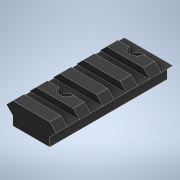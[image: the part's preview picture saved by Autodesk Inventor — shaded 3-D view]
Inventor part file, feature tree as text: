
AUTODESK INVENTOR PART (.ipt)
format: ipt  version: 2021 (Build 250183000, 183)  size: 216,064 bytes
history: native  units: mm
features: extrude x4, sketch x3, pattern_linear x2
ambient origin geometry x8: Origin, YZ Plane, XZ Plane, XY Plane, X Axis, Y Axis, Z Axis, Center Point
bodies: Solid1 (feature_tree)
feature tree (9):
  extrude  "Extrusion1"  Depth=15.67mm
  extrude  "Extrusion3"  Depth=50.0mm TaperAngle=0.0deg
  pattern_linear  "Rectangular Pattern1"  Spacing1=5.25mm  [1 undecoded]
  sketch  "Sketch3"  dims[d9=4.0mm d10=5.25mm d13=10.32mm d14=0.0mm d15=0.0mm d16=200.0mm d18=10.0mm d19=3.2mm d20=6.0mm d21=5.0mm d22=0.0mm d23=0.0mm d24=7.32mm d25=0.0mm d26=70.0mm d28=30.0mm]
  extrude  "Extrusion4"  Depth=30.0mm
  extrude  "Extrusion5"  TaperAngle=0.0deg  [1 undecoded]
  pattern_linear  "Rectangular Pattern2"  Count1=20 Spacing1=10.0mm
  sketch  "Sketch1"  dims[d0=15.67mm d1=21.21mm]
  sketch  "Sketch2"  dims[d2=3.78mm d5=50.0mm d6=0.0mm]
note: 2 required parameter values undecoded (feature->parameter linkage not recoverable at this tier; creation-order binding heuristic only, values carry confidence <= 0.55)
